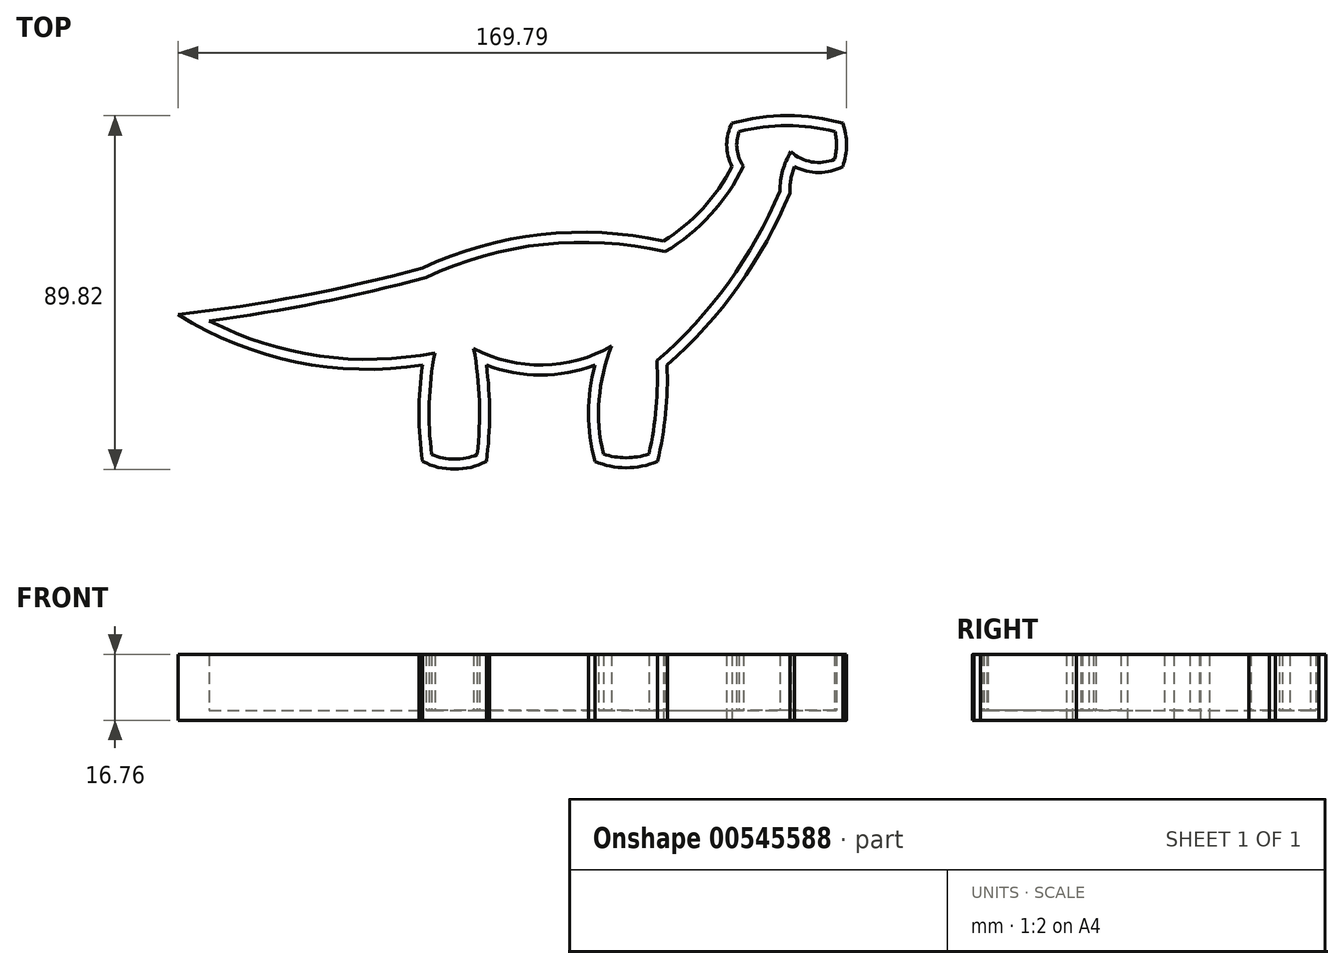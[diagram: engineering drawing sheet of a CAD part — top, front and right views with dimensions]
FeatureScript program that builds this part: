
annotation { "Feature Type Name" : "Feature", "Feature Type Description" : "" }
export const myFeature = defineFeature(function(context is Context, id is Id, definition is map)
    precondition{}
    {
        {
            var Q0;
            Q0=qCreatedBy(makeId("Top.planeOp"),FACE);
            var sketch = newSketch(context, id + "F0", { "sketchPlane" : qUnion([Q0])});
            skArc(sketch, "E0", {"start": v(-89.47, -3.5) * mm, "mid": v(-58.2, 1.23) * mm, "end": v(-27.37, 8.34) * mm});
            skArc(sketch, "E1", {"start": v(33.8, 15.17) * mm, "mid": v(2.65, 16.82) * mm, "end": v(-27.37, 8.34) * mm});
            skArc(sketch, "E2", {"start": v(-89.47, -3.5) * mm, "mid": v(-59.59, -15.55) * mm, "end": v(-27.37, -16.34) * mm});
            skArc(sketch, "E3", {"start": v(-27.37, -16.34) * mm, "mid": v(-28.29, -28.58) * mm, "end": v(-27.37, -40.81) * mm});
            skArc(sketch, "E4", {"start": v(-27.37, -40.81) * mm, "mid": v(-19.27, -42.8) * mm, "end": v(-11.16, -40.81) * mm});
            skArc(sketch, "E5", {"start": v(-11.16, -40.81) * mm, "mid": v(-10.37, -28.58) * mm, "end": v(-11.16, -16.34) * mm});
            skArc(sketch, "E6", {"start": v(-11.16, -16.34) * mm, "mid": v(2.6, -18.88) * mm, "end": v(16.37, -16.34) * mm});
            skArc(sketch, "E7", {"start": v(16.37, -16.34) * mm, "mid": v(14.8, -28.58) * mm, "end": v(16.37, -40.81) * mm});
            skArc(sketch, "E8", {"start": v(16.37, -40.81) * mm, "mid": v(24.33, -42.43) * mm, "end": v(32.28, -40.81) * mm});
            skArc(sketch, "E9", {"start": v(32.28, -40.81) * mm, "mid": v(34.36, -28.66) * mm, "end": v(34.73, -16.34) * mm});
            skArc(sketch, "E10", {"start": v(34.73, -16.34) * mm, "mid": v(52.85, 3.73) * mm, "end": v(65.93, 27.4) * mm});
            skArc(sketch, "E11", {"start": v(33.8, 15.17) * mm, "mid": v(43.8, 23.47) * mm, "end": v(51.24, 34.13) * mm});
            skArc(sketch, "E12", {"start": v(51.24, 45.14) * mm, "mid": v(49.88, 39.64) * mm, "end": v(51.24, 34.13) * mm});
            skArc(sketch, "E13", {"start": v(79.39, 45.14) * mm, "mid": v(65.32, 47.02) * mm, "end": v(51.24, 45.14) * mm});
            skArc(sketch, "E14", {"start": v(79.39, 34.13) * mm, "mid": v(80.32, 39.64) * mm, "end": v(79.39, 45.14) * mm});
            skArc(sketch, "E15", {"start": v(67.15, 34.13) * mm, "mid": v(73.27, 32.6) * mm, "end": v(79.39, 34.13) * mm});
            skArc(sketch, "E16", {"start": v(67.15, 34.13) * mm, "mid": v(66.19, 30.83) * mm, "end": v(65.93, 27.4) * mm});
            skSolve(sketch);
        }
        {
            var Q0;
            Q0 = qSketchRegion(id + "F0", true);
            extrude(context, id + "F1", {"entities" : qUnion([Q0]), "depth" : 16.76 * mm, "offsetDistance" : 25.4 * mm});
        }
        {
            var Q0;
            Q0=makeQuery(id+"F1.opExtrude","CAP_FACE",FACE,{"disambiguationData":[OSD([sQuery(id+"F0.wireOp",EDGE,"E0"),sQuery(id+"F0.wireOp",EDGE,"E1"),sQuery(id+"F0.wireOp",EDGE,"E2"),sQuery(id+"F0.wireOp",EDGE,"E3"),sQuery(id+"F0.wireOp",EDGE,"E4"),sQuery(id+"F0.wireOp",EDGE,"E5"),sQuery(id+"F0.wireOp",EDGE,"E6"),sQuery(id+"F0.wireOp",EDGE,"E7"),sQuery(id+"F0.wireOp",EDGE,"E8"),sQuery(id+"F0.wireOp",EDGE,"E9"),sQuery(id+"F0.wireOp",EDGE,"E10"),sQuery(id+"F0.wireOp",EDGE,"E11"),sQuery(id+"F0.wireOp",EDGE,"E12"),sQuery(id+"F0.wireOp",EDGE,"E13"),sQuery(id+"F0.wireOp",EDGE,"E14"),sQuery(id+"F0.wireOp",EDGE,"E15"),sQuery(id+"F0.wireOp",EDGE,"E16")])],"isStart":false});
            shell(context, id + "F2", {"entities" : qUnion([Q0]), "thickness" : 2.54 * mm});
        }
    });
